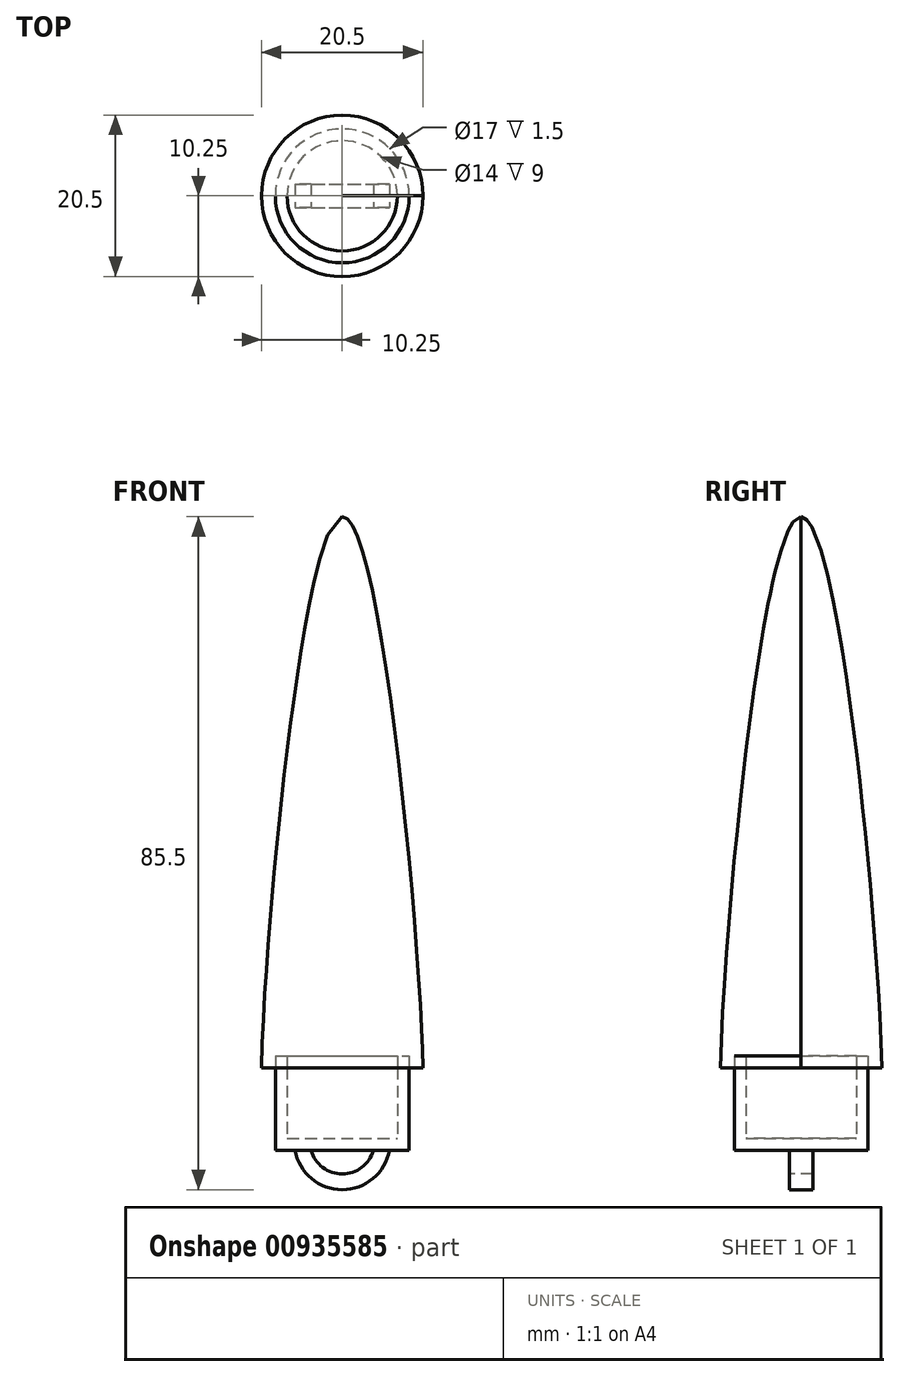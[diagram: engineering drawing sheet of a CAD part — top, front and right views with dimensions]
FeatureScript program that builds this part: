
annotation { "Feature Type Name" : "Feature", "Feature Type Description" : "" }
export const myFeature = defineFeature(function(context is Context, id is Id, definition is map)
    precondition{}
    {
        {
            var Q0;
            Q0=qCreatedBy(makeId("Front.planeOp"),FACE);
            var sketch = newSketch(context, id + "F0", { "sketchPlane" : qUnion([Q0])});
            skLineSegment(sketch, "E0", {"start": v(0, 0) * mm, "end": v(0, 70) * mm});
            skLineSegment(sketch, "E1", {"start": v(10.25, 0) * mm, "end": v(0, 0) * mm});
            skFitSpline(sketch, "E2", {"points": [v(0, 70) * mm, v(10.25, 0) * mm], "startDerivative": vector(15, 0) * mm, "endDerivative": vector(0.75, -48) * mm});
            skFitSpline(sketch, "E3.0", {"points": [v(-0.5, 68.7) * mm, v(-0.49, 68.7) * mm, v(-0.46, 68.67) * mm, v(-0.42, 68.64) * mm, v(-0.4, 68.62) * mm, v(-0.38, 68.61) * mm, v(-0.37, 68.6) * mm, v(-0.37, 68.6) * mm, v(-0.36, 68.6) * mm, v(-0.36, 68.6) * mm, v(-0.36, 68.6) * mm, v(-0.36, 68.6) * mm, v(-0.36, 68.6) * mm, v(-0.36, 68.6) * mm, v(-0.35, 68.58) * mm, v(-0.32, 68.56) * mm, v(-0.28, 68.52) * mm, v(-0.22, 68.44) * mm, v(-0.13, 68.3) * mm, v(0.01, 68.08) * mm, v(0.2, 67.72) * mm, v(0.46, 67.15) * mm, v(0.8, 66.25) * mm, v(1.23, 64.93) * mm, v(1.65, 63.38) * mm, v(2.08, 61.62) * mm, v(2.64, 59.04) * mm, v(3.33, 55.39) * mm, v(4.12, 50.47) * mm, v(4.87, 45.16) * mm, v(5.58, 39.56) * mm, v(6.24, 33.82) * mm, v(7.03, 26.12) * mm, v(7.85, 16.74) * mm, v(8.52, 6.87) * mm, v(8.72, 1.89) * mm, v(8.75, -0.02) * mm]});
            skLineSegment(sketch, "E4.bottom", {"start": v(8.5, 1.5) * mm, "end": v(7, 1.5) * mm});
            skLineSegment(sketch, "E4.top", {"start": v(8.5, -10.5) * mm, "end": v(7, -10.5) * mm});
            skLineSegment(sketch, "E4.left", {"start": v(8.5, 1.5) * mm, "end": v(8.5, -10.5) * mm});
            skLineSegment(sketch, "E4.right", {"start": v(7, 1.5) * mm, "end": v(7, -10.5) * mm});
            skPoint(sketch, "E4.middle", {"position": v(7.75, -4.5) * mm});
            skLineSegment(sketch, "E5.bottom", {"start": v(7, -10.5) * mm, "end": v(0, -10.5) * mm});
            skLineSegment(sketch, "E5.top", {"start": v(7, -9) * mm, "end": v(0, -9) * mm});
            skLineSegment(sketch, "E5.left", {"start": v(7, -10.5) * mm, "end": v(7, -9) * mm});
            skLineSegment(sketch, "E5.right", {"start": v(0, -10.5) * mm, "end": v(0, -9) * mm});
            skSolve(sketch);
        }
        {
            var Q0;
            {var subQ5=sQuery(id+"F0.wireOp",EDGE,"E2");Q0=makeQuery(id+"F0.imprint","IMPRINT",FACE,{"disambiguationData":[TD([[makeQuery(id+"F0.imprint","IMPRINT",EDGE,{"derivedFrom":subQ5}),-1.0]])]});}
            var Q1;
            {var subQ1=sQuery(id+"F0.wireOp",EDGE,"E0");var subQ7=sQuery(id+"F0.wireOp",EDGE,"E1");var subQ8=makeQuery(id+"F0.imprint","INTERSECT",VERTEX,{"derivedFrom":[subQ1,subQ7]});Q1=makeQuery(id+"F0.imprint","IMPRINT",FACE,{"disambiguationData":[TD([[makeQuery(id+"F0.imprint","IMPRINT",EDGE,{"disambiguationData":[TD([[subQ8,-1.0]])],"derivedFrom":subQ1}),-1.0]])]});}
            var Q2;
            {var subQ0=sQuery(id+"F0.wireOp",EDGE,"E4.top");Q2=makeQuery(id+"F0.imprint","IMPRINT",FACE,{"disambiguationData":[TD([[makeQuery(id+"F0.imprint","IMPRINT",EDGE,{"derivedFrom":subQ0}),-1.0]])]});}
            var Q3;
            Q3=makeQuery(id+"F0.imprint","IMPRINT",FACE,{"disambiguationData":[TD([[makeQuery(id+"F0.imprint","IMPRINT",EDGE,{"derivedFrom":sQuery(id+"F0.wireOp",EDGE,"E5.bottom")}),-1.0]])]});
            var Q4;
            Q4=sQuery(id+"F0.wireOp",EDGE,"E0");
            revolve(context, id + "F1", {"surfaceOperationType" : NewSurfaceOperationType.NEW, "entities" : qUnion([Q0, Q1, Q2, Q3]), "axis" : qUnion([Q4]), "revolveType" : RevolveType.FULL});
        }
        {
            var Q0;
            Q0=qCreatedBy(makeId("Front.planeOp"),FACE);
            var sketch = newSketch(context, id + "F2", { "sketchPlane" : qUnion([Q0])});
            skArc(sketch, "E6", {"start": v(-6, -10.5) * mm, "mid": v(0, -15.5) * mm, "end": v(6, -10.5) * mm});
            skArc(sketch, "E7.0", {"start": v(-3.95, -10.5) * mm, "mid": v(0, -13.5) * mm, "end": v(3.95, -10.5) * mm});
            skLineSegment(sketch, "E8.0.0", {"start": v(6, -10.5) * mm, "end": v(3.95, -10.5) * mm});
            skPoint(sketch, "E9.orphan", {"position": v(-3.65, -4.52) * mm});
            skPoint(sketch, "E10.orphan", {"position": v(6.1, -9.3) * mm});
            skPoint(sketch, "E11.orphan", {"position": v(8.5, -10.5) * mm});
            skLineSegment(sketch, "E12.trimOffspring", {"start": v(-3.95, -10.5) * mm, "end": v(-6, -10.5) * mm});
            skPoint(sketch, "E13.orphan", {"position": v(-8.5, -10.5) * mm});
            skSolve(sketch);
        }
        {
            var Q0;
            Q0 = qSketchRegion(id + "F2", true);
            extrude(context, id + "F3", {"entities" : qUnion([Q0]), "operationType" : NewBodyOperationType.ADD, "oppositeDirection" : true, "depth" : 1.5 * mm, "offsetDistance" : 25 * mm, "hasSecondDirection" : true, "secondDirectionOppositeDirection" : false, "secondDirectionDepth" : 1.5 * mm});
        }
    });
